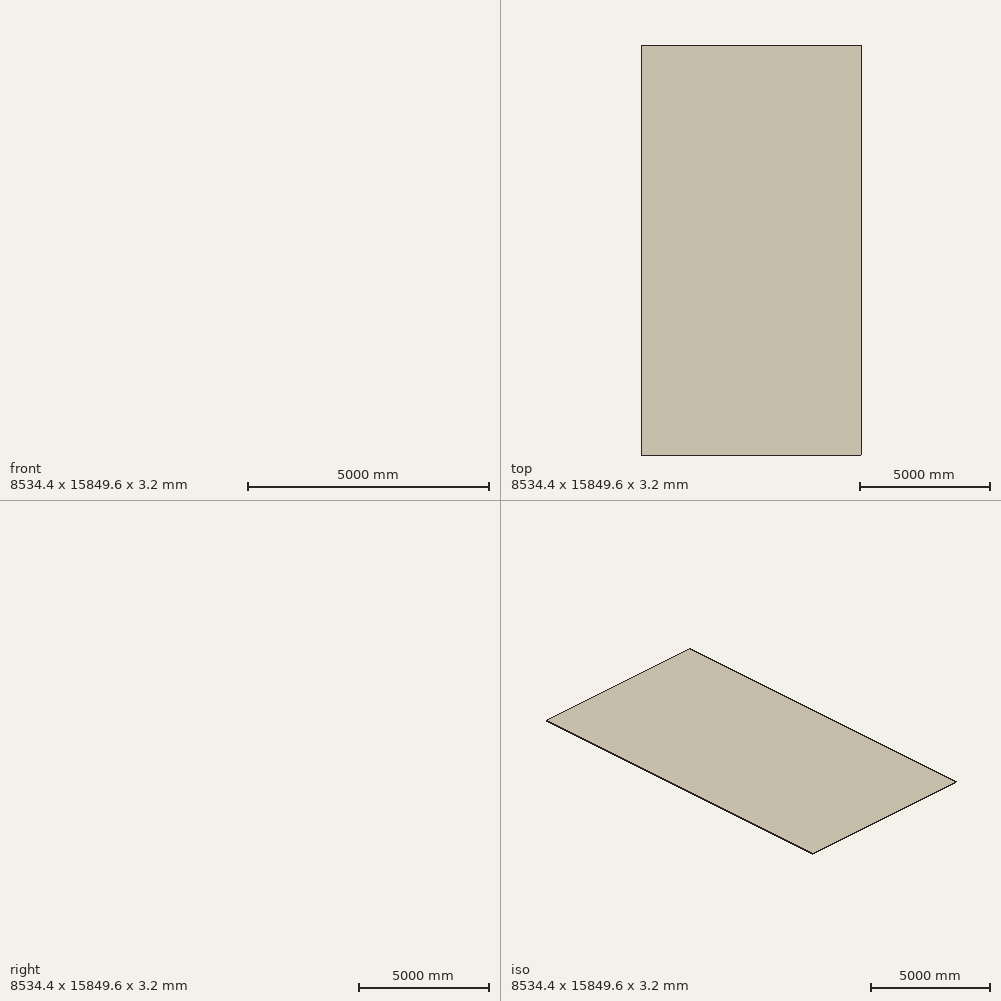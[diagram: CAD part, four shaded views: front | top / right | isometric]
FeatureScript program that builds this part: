
annotation { "Feature Type Name" : "Feature", "Feature Type Description" : "" }
export const myFeature = defineFeature(function(context is Context, id is Id, definition is map)
    precondition{}
    {
        {
            var Q0;
            Q0=qCreatedBy(makeId("Top.planeOp"),FACE);
            var sketch = newSketch(context, id + "F0", { "sketchPlane" : qUnion([Q0])});
            skLineSegment(sketch, "E0.bottom", {"start": v(4267.2, -7924.8) * mm, "end": v(-4267.2, -7924.8) * mm});
            skLineSegment(sketch, "E0.top", {"start": v(4267.2, 7924.8) * mm, "end": v(-4267.2, 7924.8) * mm});
            skLineSegment(sketch, "E0.left", {"start": v(4267.2, -7924.8) * mm, "end": v(4267.2, 7924.8) * mm});
            skLineSegment(sketch, "E0.right", {"start": v(-4267.2, -7924.8) * mm, "end": v(-4267.2, 7924.8) * mm});
            skPoint(sketch, "E0.middle", {"position": v(0, 0) * mm});
            skSolve(sketch);
        }
        {
            var Q0;
            Q0=makeQuery(id+"F0.imprint","IMPRINT",FACE,{"disambiguationData":[TD([[makeQuery(id+"F0.imprint","IMPRINT",EDGE,{"derivedFrom":sQuery(id+"F0.wireOp",EDGE,"E0.bottom")}),-1.0]])]});
            extrude(context, id + "F1", {"entities" : qUnion([Q0]), "depth" : 3.17 * mm});
        }
    });
